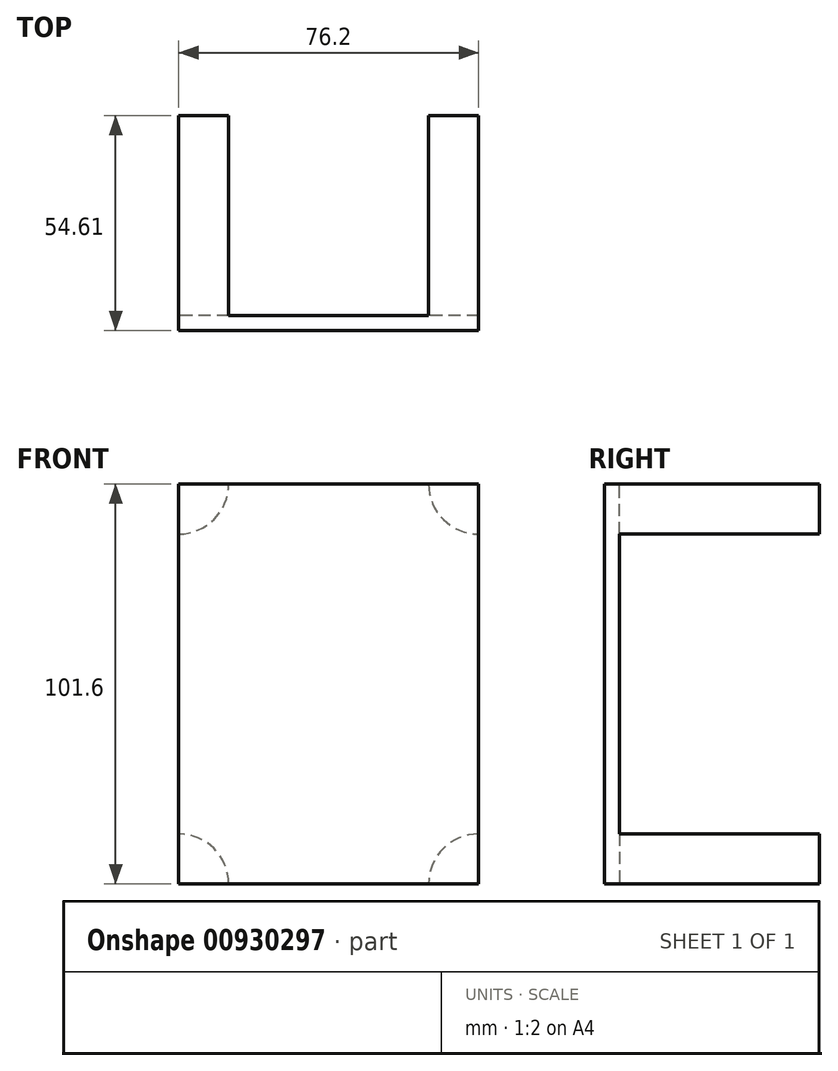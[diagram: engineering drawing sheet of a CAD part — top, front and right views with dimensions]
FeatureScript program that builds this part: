
annotation { "Feature Type Name" : "Feature", "Feature Type Description" : "" }
export const myFeature = defineFeature(function(context is Context, id is Id, definition is map)
    precondition{}
    {
        {
            var Q0;
            Q0=qCreatedBy(makeId("Front.planeOp"),FACE);
            var sketch = newSketch(context, id + "F0", { "sketchPlane" : qUnion([Q0])});
            skLineSegment(sketch, "E0.bottom", {"start": v(-33.46, -50.38) * mm, "end": v(42.74, -50.38) * mm});
            skLineSegment(sketch, "E0.top", {"start": v(-33.46, 51.22) * mm, "end": v(42.74, 51.22) * mm});
            skLineSegment(sketch, "E0.left", {"start": v(-33.46, -50.38) * mm, "end": v(-33.46, 51.22) * mm});
            skLineSegment(sketch, "E0.right", {"start": v(42.74, -50.38) * mm, "end": v(42.74, 51.22) * mm});
            skSolve(sketch);
        }
        {
            var Q0;
            Q0 = qSketchRegion(id + "F0", true);
            extrude(context, id + "F1", {"entities" : qUnion([Q0]), "depth" : 3.8 * mm, "offsetDistance" : 25.4 * mm});
        }
        {
            var Q0;
            Q0=makeQuery(id+"F1.opExtrude","CAP_FACE",FACE,{"disambiguationData":[OSD([sQuery(id+"F0.wireOp",EDGE,"E0.bottom"),sQuery(id+"F0.wireOp",EDGE,"E0.top"),sQuery(id+"F0.wireOp",EDGE,"E0.left"),sQuery(id+"F0.wireOp",EDGE,"E0.right")])],"isStart":true});
            var sketch = newSketch(context, id + "F2", { "sketchPlane" : qUnion([Q0])});
            skLineSegment(sketch, "E1.bottom", {"start": v(33.46, -50.38) * mm, "end": v(20.76, -50.38) * mm});
            skLineSegment(sketch, "E1.top", {"start": v(33.46, -37.68) * mm, "end": v(20.76, -37.68) * mm});
            skLineSegment(sketch, "E1.left", {"start": v(33.46, -50.38) * mm, "end": v(33.46, -37.68) * mm});
            skLineSegment(sketch, "E1.right", {"start": v(20.76, -50.38) * mm, "end": v(20.76, -37.68) * mm});
            skLineSegment(sketch, "E2.bottom", {"start": v(-42.74, 51.22) * mm, "end": v(-30.04, 51.22) * mm});
            skLineSegment(sketch, "E2.top", {"start": v(-42.74, 38.52) * mm, "end": v(-30.04, 38.52) * mm});
            skLineSegment(sketch, "E2.left", {"start": v(-42.74, 51.22) * mm, "end": v(-42.74, 38.52) * mm});
            skLineSegment(sketch, "E2.right", {"start": v(-30.04, 51.22) * mm, "end": v(-30.04, 38.52) * mm});
            skLineSegment(sketch, "E3.bottom", {"start": v(33.46, 51.22) * mm, "end": v(20.76, 51.22) * mm});
            skLineSegment(sketch, "E3.top", {"start": v(33.46, 38.52) * mm, "end": v(20.76, 38.52) * mm});
            skLineSegment(sketch, "E3.left", {"start": v(33.46, 51.22) * mm, "end": v(33.46, 38.52) * mm});
            skLineSegment(sketch, "E3.right", {"start": v(20.76, 51.22) * mm, "end": v(20.76, 38.52) * mm});
            skLineSegment(sketch, "E4.bottom", {"start": v(-42.74, -50.38) * mm, "end": v(-30.04, -50.38) * mm});
            skLineSegment(sketch, "E4.top", {"start": v(-42.74, -37.68) * mm, "end": v(-30.04, -37.68) * mm});
            skLineSegment(sketch, "E4.left", {"start": v(-42.74, -50.38) * mm, "end": v(-42.74, -37.68) * mm});
            skLineSegment(sketch, "E4.right", {"start": v(-30.04, -50.38) * mm, "end": v(-30.04, -37.68) * mm});
            skSolve(sketch);
        }
        {
            var Q0;
            Q0 = qSketchRegion(id + "F2", true);
            extrude(context, id + "F3", {"entities" : qUnion([Q0]), "operationType" : NewBodyOperationType.ADD, "depth" : 50.8 * mm, "offsetDistance" : 25.4 * mm});
        }
        {
            var Q0;
            Q0=makeQuery(id+"F3.opExtrude","SWEPT_EDGE",EDGE,{"disambiguationData":[OSD([sQuery(id+"F2.wireOp",EDGE,"E3.top"),sQuery(id+"F2.wireOp",EDGE,"E3.right")])]});
            var Q1;
            Q1=makeQuery(id+"F3.opExtrude","SWEPT_EDGE",EDGE,{"disambiguationData":[OSD([sQuery(id+"F2.wireOp",EDGE,"E1.top"),sQuery(id+"F2.wireOp",EDGE,"E1.right")])]});
            var Q2;
            Q2=makeQuery(id+"F3.opExtrude","SWEPT_EDGE",EDGE,{"disambiguationData":[OSD([sQuery(id+"F2.wireOp",EDGE,"E4.top"),sQuery(id+"F2.wireOp",EDGE,"E4.right")])]});
            var Q3;
            Q3=makeQuery(id+"F3.opExtrude","SWEPT_EDGE",EDGE,{"disambiguationData":[OSD([sQuery(id+"F2.wireOp",EDGE,"E2.top"),sQuery(id+"F2.wireOp",EDGE,"E2.right")])]});
            fillet(context, id + "F4", {"entities" : qUnion([Q0, Q1, Q2, Q3]), "radius" : 12.7 * mm, "tangentPropagation" : true, "allowEdgeOverflow" : false});
        }
    });
